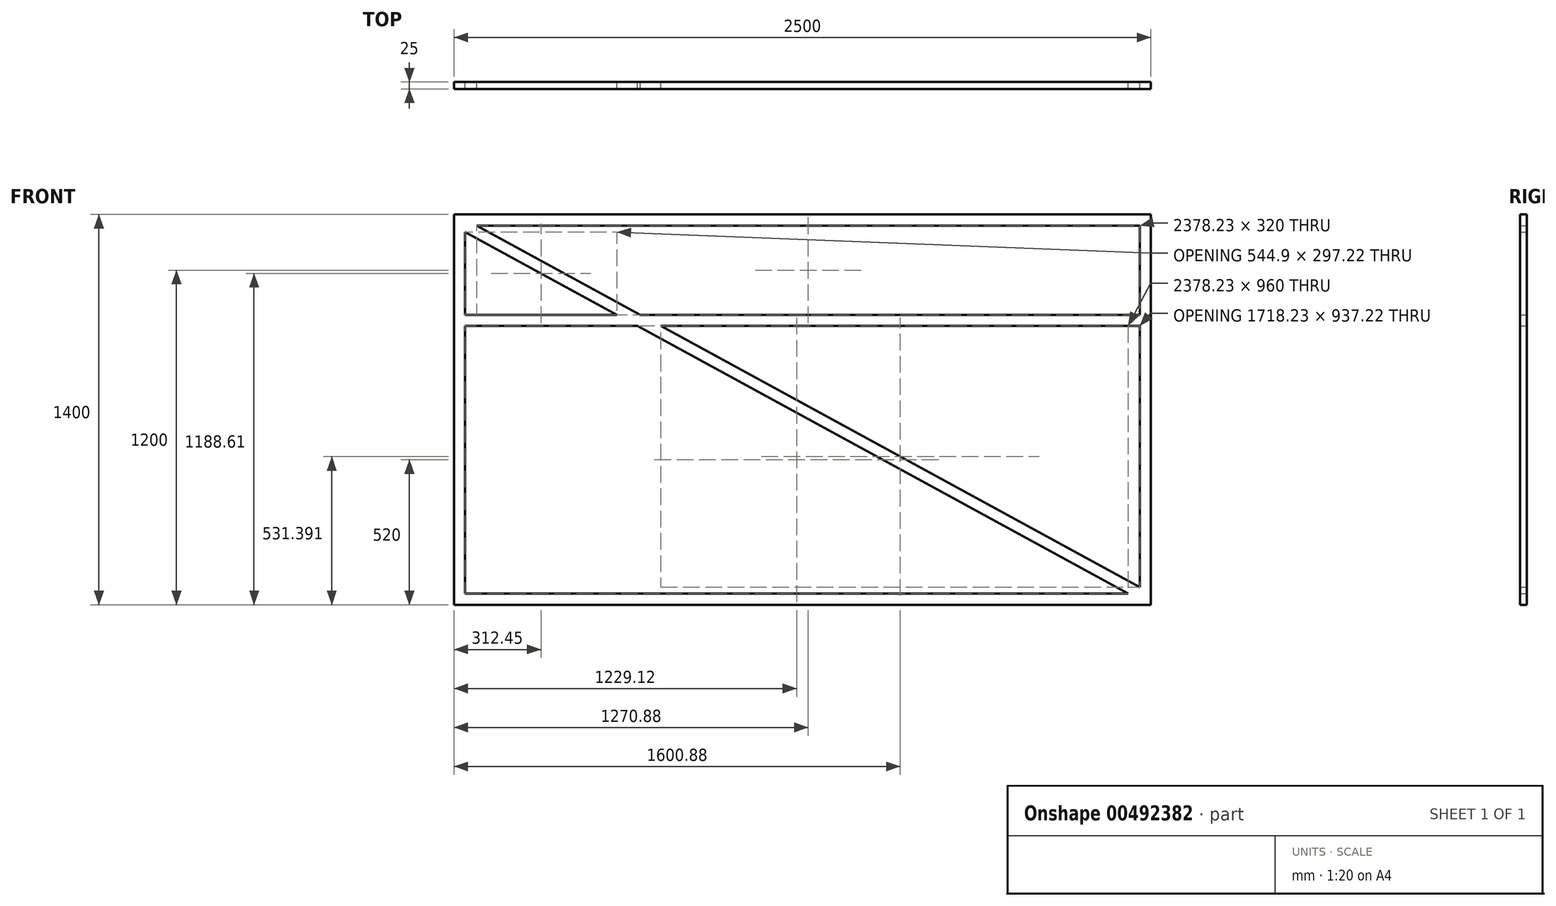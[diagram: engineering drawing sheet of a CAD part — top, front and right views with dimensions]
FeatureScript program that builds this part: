
annotation { "Feature Type Name" : "Feature", "Feature Type Description" : "" }
export const myFeature = defineFeature(function(context is Context, id is Id, definition is map)
    precondition{}
    {
        {
            var Q0;
            Q0=qCreatedBy(makeId("Front.planeOp"),FACE);
            var sketch = newSketch(context, id + "F0", { "sketchPlane" : qUnion([Q0])});
            skLineSegment(sketch, "E0.bottom", {"start": v(0, 0) * mm, "end": v(2500, 0) * mm});
            skLineSegment(sketch, "E0.top", {"start": v(0, 1400) * mm, "end": v(2500, 1400) * mm});
            skLineSegment(sketch, "E0.left", {"start": v(0, 0) * mm, "end": v(0, 1400) * mm});
            skLineSegment(sketch, "E0.right", {"start": v(2500, 0) * mm, "end": v(2500, 1400) * mm});
            skLineSegment(sketch, "E1.0", {"start": v(40, 1360) * mm, "end": v(2460, 1360) * mm});
            skLineSegment(sketch, "E1.1", {"start": v(40, 40) * mm, "end": v(40, 1360) * mm});
            skLineSegment(sketch, "E1.2", {"start": v(40, 40) * mm, "end": v(2460, 40) * mm});
            skLineSegment(sketch, "E1.3", {"start": v(2460, 40) * mm, "end": v(2460, 1360) * mm});
            skLineSegment(sketch, "E2", {"start": v(40, 1040) * mm, "end": v(2460, 1040) * mm});
            skLineSegment(sketch, "E3.0", {"start": v(40, 1000) * mm, "end": v(2460, 1000) * mm});
            skLineSegment(sketch, "E4", {"start": v(40, 1360) * mm, "end": v(2460, 40) * mm, "construction": true});
            skLineSegment(sketch, "E5.0", {"start": v(40, 1337.22) * mm, "end": v(2418.23, 40) * mm});
            skLineSegment(sketch, "E6.0", {"start": v(81.77, 1360) * mm, "end": v(2460, 62.78) * mm});
            skSolve(sketch);
        }
        {
            var Q0;
            {var subQ1=sQuery(id+"F0.wireOp",EDGE,"E1.1");var subQ7=sQuery(id+"F0.wireOp",EDGE,"E1.0");var subQ8=makeQuery(id+"F0.imprint","INTERSECT",VERTEX,{"derivedFrom":[subQ7,subQ1]});Q0=makeQuery(id+"F0.imprint","IMPRINT",FACE,{"disambiguationData":[TD([[makeQuery(id+"F0.imprint","IMPRINT",EDGE,{"disambiguationData":[TD([[subQ8,-1.0]])],"derivedFrom":subQ7}),-1.0]])]});}
            var Q1;
            {var subQ0=sQuery(id+"F0.wireOp",EDGE,"E2");var subQ1=sQuery(id+"F0.wireOp",EDGE,"E1.1");var subQ2=makeQuery(id+"F0.imprint","INTERSECT",VERTEX,{"derivedFrom":[subQ1,subQ0]});Q1=makeQuery(id+"F0.imprint","IMPRINT",FACE,{"disambiguationData":[TD([[makeQuery(id+"F0.imprint","IMPRINT",EDGE,{"disambiguationData":[TD([[subQ2,1.0]])],"derivedFrom":subQ1}),-1.0]])]});}
            var Q2;
            {var subQ0=sQuery(id+"F0.wireOp",EDGE,"E5.0");var subQ1=sQuery(id+"F0.wireOp",EDGE,"E2");var subQ2=makeQuery(id+"F0.imprint","INTERSECT",VERTEX,{"derivedFrom":[subQ1,subQ0]});Q2=makeQuery(id+"F0.imprint","IMPRINT",FACE,{"disambiguationData":[TD([[makeQuery(id+"F0.imprint","IMPRINT",EDGE,{"disambiguationData":[TD([[subQ2,-1.0]])],"derivedFrom":subQ1}),-1.0]])]});}
            var Q3;
            {var subQ0=sQuery(id+"F0.wireOp",EDGE,"E2");var subQ1=sQuery(id+"F0.wireOp",EDGE,"E1.3");var subQ2=makeQuery(id+"F0.imprint","INTERSECT",VERTEX,{"derivedFrom":[subQ1,subQ0]});Q3=makeQuery(id+"F0.imprint","IMPRINT",FACE,{"disambiguationData":[TD([[makeQuery(id+"F0.imprint","IMPRINT",EDGE,{"disambiguationData":[TD([[subQ2,1.0]])],"derivedFrom":subQ1}),1.0]])]});}
            var Q4;
            {var subQ1=sQuery(id+"F0.wireOp",EDGE,"E1.2");var subQ7=sQuery(id+"F0.wireOp",EDGE,"E1.3");var subQ8=makeQuery(id+"F0.imprint","INTERSECT",VERTEX,{"derivedFrom":[subQ1,subQ7]});Q4=makeQuery(id+"F0.imprint","IMPRINT",FACE,{"disambiguationData":[TD([[makeQuery(id+"F0.imprint","IMPRINT",EDGE,{"disambiguationData":[TD([[subQ8,1.0]])],"derivedFrom":subQ1}),1.0]])]});}
            var Q5;
            Q5=makeQuery(id+"F0.imprint","IMPRINT",FACE,{"disambiguationData":[TD([[makeQuery(id+"F0.imprint","IMPRINT",EDGE,{"derivedFrom":sQuery(id+"F0.wireOp",EDGE,"E0.bottom")}),1.0]])]});
            extrude(context, id + "F1", {"entities" : qUnion([Q0, Q1, Q2, Q3, Q4, Q5]), "depth" : 25 * mm});
        }
    });
